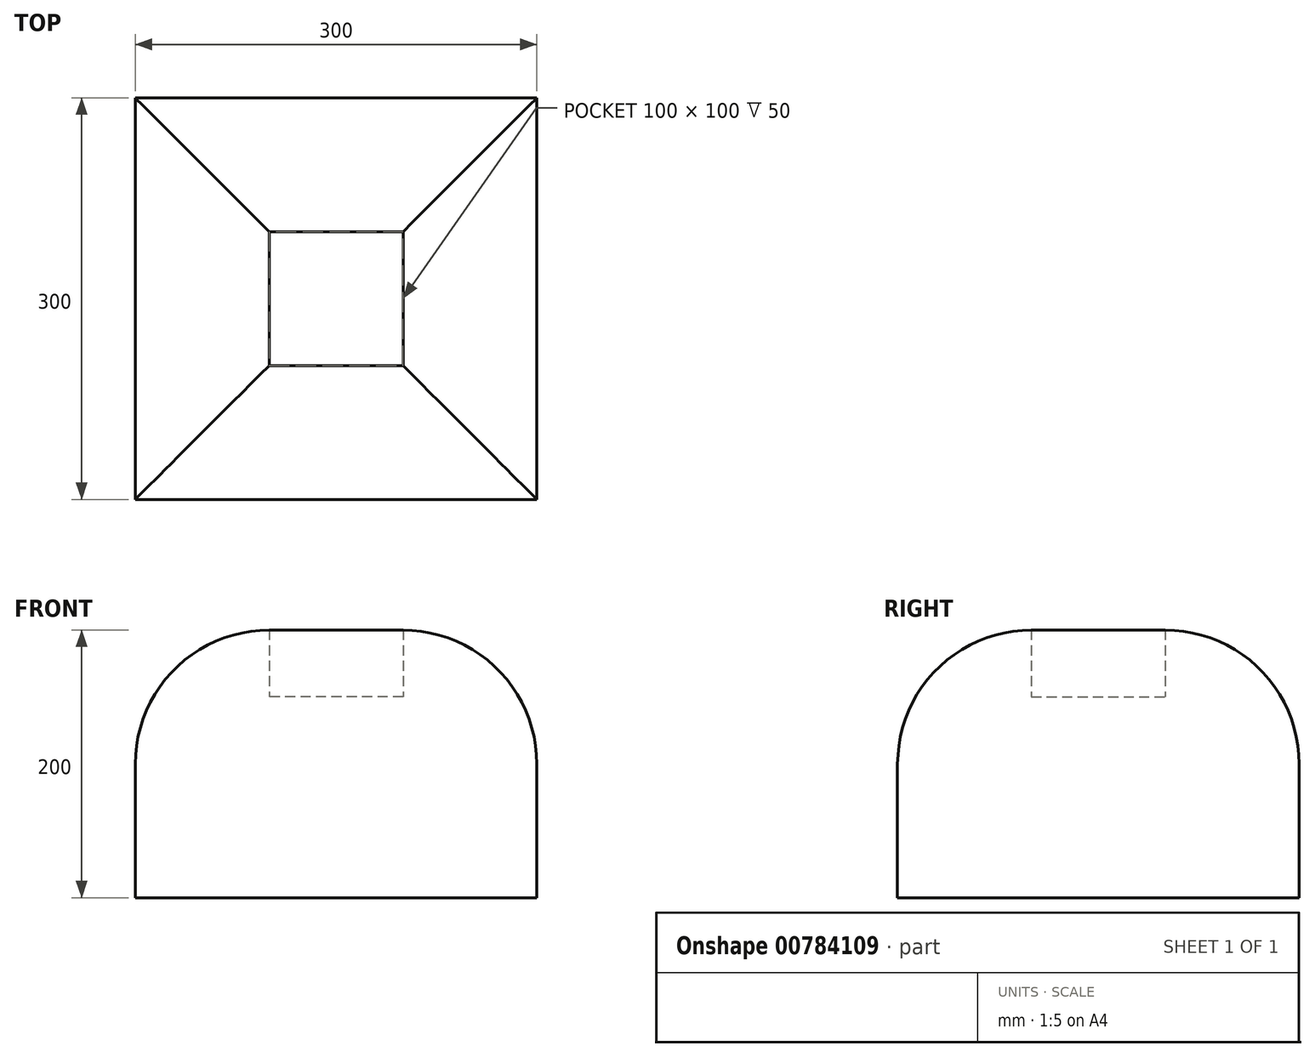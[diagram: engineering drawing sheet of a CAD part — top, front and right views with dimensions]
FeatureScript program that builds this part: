
annotation { "Feature Type Name" : "Feature", "Feature Type Description" : "" }
export const myFeature = defineFeature(function(context is Context, id is Id, definition is map)
    precondition{}
    {
        {
            var Q0;
            Q0=qCreatedBy(makeId("Top.planeOp"),FACE);
            var sketch = newSketch(context, id + "F0", { "sketchPlane" : qUnion([Q0])});
            skLineSegment(sketch, "E0.bottom", {"start": v(150, -150) * mm, "end": v(-150, -150) * mm});
            skLineSegment(sketch, "E0.top", {"start": v(150, 150) * mm, "end": v(-150, 150) * mm});
            skLineSegment(sketch, "E0.left", {"start": v(150, -150) * mm, "end": v(150, 150) * mm});
            skLineSegment(sketch, "E0.right", {"start": v(-150, -150) * mm, "end": v(-150, 150) * mm});
            skPoint(sketch, "E0.middle", {"position": v(0, 0) * mm});
            skLineSegment(sketch, "E1.0", {"start": v(50, 50) * mm, "end": v(-50, 50) * mm});
            skLineSegment(sketch, "E1.1", {"start": v(50, -50) * mm, "end": v(50, 50) * mm});
            skLineSegment(sketch, "E1.2", {"start": v(50, -50) * mm, "end": v(-50, -50) * mm});
            skLineSegment(sketch, "E1.3", {"start": v(-50, -50) * mm, "end": v(-50, 50) * mm});
            skSolve(sketch);
        }
        {
            var Q0;
            Q0=makeQuery(id+"F0.imprint","IMPRINT",FACE,{"disambiguationData":[TD([[makeQuery(id+"F0.imprint","IMPRINT",EDGE,{"derivedFrom":sQuery(id+"F0.wireOp",EDGE,"E0.bottom")}),-1.0]])]});
            extrude(context, id + "F1", {"entities" : qUnion([Q0]), "depth" : 200 * mm, "offsetDistance" : 25 * mm});
        }
        {
            var Q0;
            Q0=makeQuery(id+"F0.imprint","IMPRINT",FACE,{"disambiguationData":[TD([[makeQuery(id+"F0.imprint","IMPRINT",EDGE,{"derivedFrom":sQuery(id+"F0.wireOp",EDGE,"E1.0")}),1.0]])]});
            extrude(context, id + "F2", {"entities" : qUnion([Q0]), "operationType" : NewBodyOperationType.ADD, "depth" : 150 * mm, "offsetDistance" : 25 * mm});
        }
        {
            var Q0;
            Q0=makeQuery(id+"F1.opExtrude","CAP_EDGE",EDGE,{"disambiguationData":[OSD([sQuery(id+"F0.wireOp",EDGE,"E0.right")])],"isStart":false});
            var Q1;
            Q1=makeQuery(id+"F1.opExtrude","CAP_EDGE",EDGE,{"disambiguationData":[OSD([sQuery(id+"F0.wireOp",EDGE,"E0.bottom")])],"isStart":false});
            var Q2;
            Q2=makeQuery(id+"F1.opExtrude","CAP_EDGE",EDGE,{"disambiguationData":[OSD([sQuery(id+"F0.wireOp",EDGE,"E0.left")])],"isStart":false});
            var Q3;
            Q3=makeQuery(id+"F1.opExtrude","CAP_EDGE",EDGE,{"disambiguationData":[OSD([sQuery(id+"F0.wireOp",EDGE,"E0.top")])],"isStart":false});
            fillet(context, id + "F3", {"entities" : qUnion([Q0, Q1, Q2, Q3]), "radius" : 100 * mm, "tangentPropagation" : true, "allowEdgeOverflow" : false});
        }
    });
